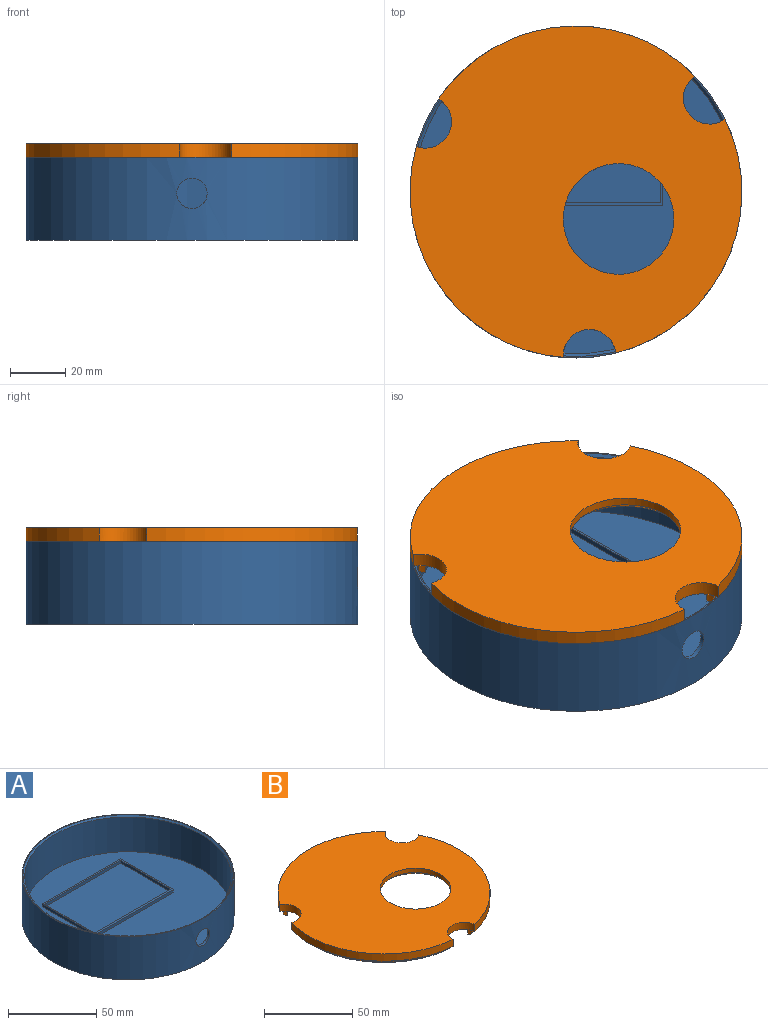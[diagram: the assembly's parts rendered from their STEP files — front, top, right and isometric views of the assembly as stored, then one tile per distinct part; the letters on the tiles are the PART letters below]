
ASSEMBLY  parts=2 mates=1
PART A: 17 faces, bbox 120x120x30 mm
  f0: plane 117x117mm, normal (0,0,1), area 8095.1mm2, adj f2,f9,f10,f11,f12
  f1: cylinder r=60mm len=120mm, axis (0,0,1), area 11214.2mm2, adj f3,f4,f5
  f2: cylinder r=58.5mm len=117mm, axis (0,0,-1), area 8726.3mm2, adj f0,f5,f16
  f3: plane 120x120mm, normal (0,0,-1), area 11309.7mm2, adj f1
  f4: plane 120x120mm, normal (0,0,1), area 187.7mm2, adj f1,f16
  f5: cylinder r=5.5mm len=11mm, axis (0,1,0), area 51.9mm2, adj f1,f2
  f6: plane 61x2mm, normal (0,-1,0), area 122mm2, adj f7,f13,f14,f15
  f7: plane 40x2mm, normal (-1,0,0), area 80mm2, adj f6,f8,f14,f15
  f8: plane 61x2mm, normal (0,1,0), area 122mm2, adj f7,f13,f14,f15
  f9: plane 42.5x2mm, normal (1,0,0), area 85mm2, adj f0,f10,f12,f14
  f10: plane 62.5x2mm, normal (0,1,0), area 125mm2, adj f0,f9,f11,f14
  f11: plane 42.5x2mm, normal (-1,0,0), area 85mm2, adj f0,f10,f12,f14
  f12: plane 62.5x2mm, normal (0,-1,0), area 125mm2, adj f0,f9,f11,f14
  f13: plane 40x2mm, normal (1,0,0), area 80mm2, adj f6,f8,f14,f15
  f14: plane 62.5x42.5mm, normal (0,0,1), area 216.3mm2, adj f6,f7,f8,f9,f10,f11,f12,f13
  f15: plane 61x40mm, normal (0,0,1), area 2440mm2, adj f6,f7,f8,f13
  f16: cone r=58.5mm half-angle=45deg, axis (0,0,1), area 524.3mm2, adj f2,f4
PART B: 32 faces, bbox 120x119.8x8 mm
  f0: plane 120x115.33mm, normal (0,0,-1), area 8383.8mm2, adj f2,f4,f5,f6,f8,f10,f11,f12
  f1: plane 92.71x27.6mm, normal (0,0,-1), area 209.3mm2, adj f2,f3,f4,f19
  f2: cylinder r=9.5mm len=17.35mm, axis (0,0,-1), area 150.6mm2, adj f0,f1,f3,f8,f9,f15
  f3: cylinder r=60mm len=92.71mm, axis (0,0,-1), area 532.7mm2, adj f1,f2,f4,f9
  f4: cylinder r=9.5mm len=17.74mm, axis (0,0,-1), area 141.1mm2, adj f0,f1,f3,f5,f9,f16
  f5: cylinder r=60mm len=76.24mm, axis (0,0,-1), area 531.6mm2, adj f0,f4,f6,f9
  f6: cylinder r=9.5mm len=18.95mm, axis (0,0,-1), area 147.4mm2, adj f0,f5,f8,f9,f22
  f7: cylinder r=20mm len=40mm, axis (0,0,-1), area 377mm2, adj f9,f31
  f8: cylinder r=60mm len=84.58mm, axis (0,0,-1), area 534.9mm2, adj f0,f2,f6,f9
  f9: plane 120x119.83mm, normal (0,0,1), area 9615.4mm2, adj f2,f3,f4,f5,f6,f7,f8
  f10: cylinder r=55.5mm len=71.27mm, axis (0,0,1), area 298.6mm2, adj f0,f11,f13,f14
  f11: cylinder r=9.5mm len=3mm, axis (0,0,1), area 7.3mm2, adj f0,f10,f12,f14,f30
  f12: cylinder r=58mm len=73.72mm, axis (0,0,1), area 205.4mm2, adj f0,f11,f13,f30
  f13: cylinder r=9.5mm len=3mm, axis (0,0,1), area 7.2mm2, adj f0,f10,f12,f14,f30
  f14: plane 72.74x53.21mm, normal (0,0,-1), area 150.5mm2, adj f10,f11,f13,f30
  f15: plane 2.09x1.54mm, normal (0,0,1), area 0.1mm2, adj f2,f17,f18,f19
  f16: plane 2.03x1.71mm, normal (0,0,1), area 0.1mm2, adj f4,f17,f19,f20
  f17: cylinder r=55.5mm len=86.46mm, axis (0,0,1), area 299.1mm2, adj f0,f15,f16,f18,f20,f21
  f18: cylinder r=9.5mm len=3mm, axis (0,0,1), area 7.1mm2, adj f15,f17,f19,f21,f28
  f19: cylinder r=58mm len=89.64mm, axis (0,0,1), area 206.1mm2, adj f1,f15,f16,f18,f20,f28
  f20: cylinder r=9.5mm len=3mm, axis (0,0,1), area 7.3mm2, adj f16,f17,f19,f21,f28
  f21: plane 88.26x26.63mm, normal (0,0,-1), area 150.9mm2, adj f17,f18,f20,f28
  f22: plane 2.32x1.18mm, normal (0,0,1), area 0.2mm2, adj f6,f23,f24,f25
  f23: cylinder r=55.5mm len=78.53mm, axis (0,0,1), area 299mm2, adj f0,f22,f24,f26,f27
  f24: cylinder r=9.5mm len=3mm, axis (0,0,1), area 7.2mm2, adj f22,f23,f25,f27,f29
  f25: cylinder r=58mm len=81.55mm, axis (0,0,1), area 206.4mm2, adj f0,f22,f24,f26,f29
  f26: cylinder r=9.5mm len=3mm, axis (0,0,1), area 7.1mm2, adj f0,f23,f25,f27,f29
  f27: plane 80.25x44.22mm, normal (0,0,-1), area 150.9mm2, adj f23,f24,f26,f29
  f28: cone r=58mm half-angle=45deg, axis (0,0,1), area 144.6mm2, adj f18,f19,f20,f21
  f29: cone r=58mm half-angle=45deg, axis (0,0,1), area 144.8mm2, adj f24,f25,f26,f27
  f30: cone r=58mm half-angle=45deg, axis (0,0,1), area 144.2mm2, adj f11,f12,f13,f14
  f31: cone r=22mm half-angle=45deg, axis (0,0,-1), area 373.2mm2, adj f0,f7
PLACE A t=(-12.55,-9.3,-13.08)mm
PLACE B t=(-12.55,-9.3,11.92)mm
MATE slider B.f5 <-> A.f1  axis (0,0,-1) through (-12.55,-9.3,11.92)mm
